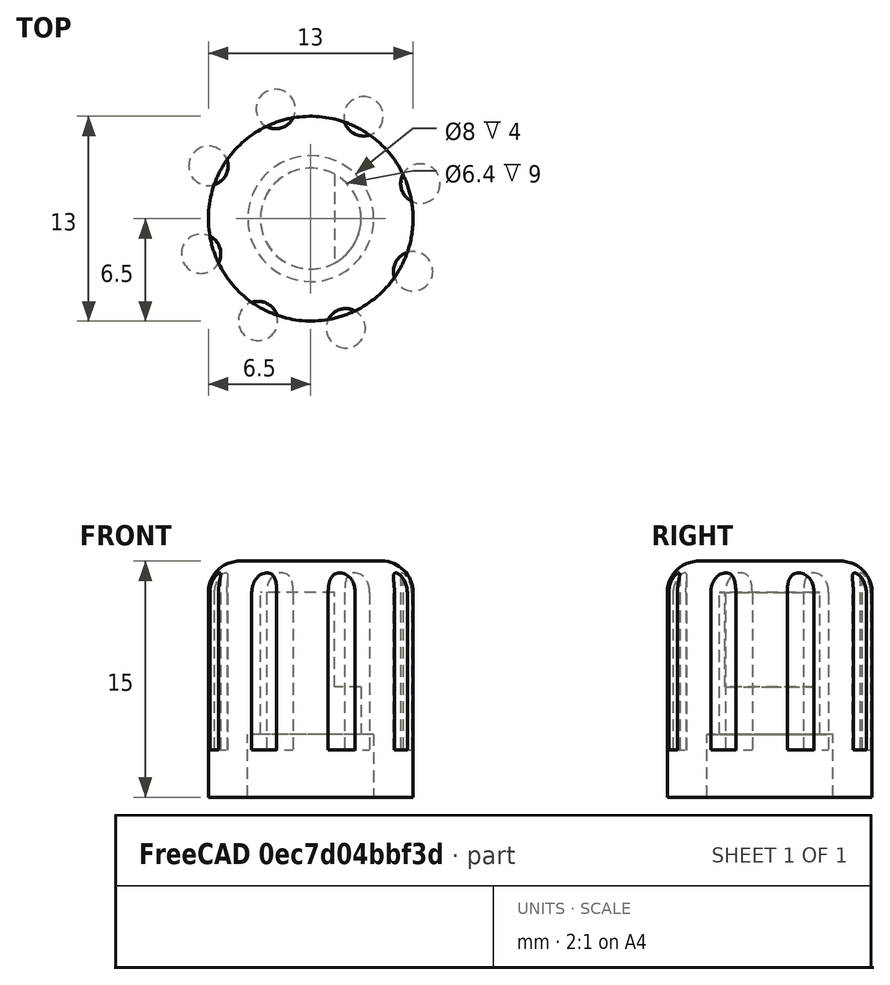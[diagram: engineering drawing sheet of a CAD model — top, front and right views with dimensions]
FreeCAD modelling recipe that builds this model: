
FCSTD DOCUMENT  (FreeCAD 0.21R33771 (Git))
Label: knob
License: All rights reserved
LicenseURL: http://en.wikipedia.org/wiki/All_rights_reserved
objects: PartDesign::SubtractiveCylinder×3, PartDesign::AdditiveCylinder×1, PartDesign::AdditiveBox×1, PartDesign::Fillet×1, PartDesign::PolarPattern×1, PartDesign::Body×1
note: 14 computed .brp shape members not serialized (recipe doc carries the construction recipe); baked Part::Feature solids carry a one-line shape summary decoded from their .brp

FEATURE [PartDesign::AdditiveCylinder] Cylinder
  Angle = 360
  AttacherType = Attacher::AttachEngine3D
  FirstAngle = 0
  Height = 15
  Radius = 6.5
  SecondAngle = 0
FEATURE [PartDesign::SubtractiveCylinder] Cylinder001
  Angle = 360
  AttacherType = Attacher::AttachEngine3D
  AttachmentOffset = pos=(0,0,-13) rot=(0,0,1;0rad)
  BaseFeature = -> Cylinder
  FirstAngle = 0
  Height = 13
  MapMode = 5
  Placement = pos=(0,0,13) rot=(1,0,0;3.14159rad)
  Radius = 3.2
  SecondAngle = 0
  Support = -> [Cylinder]
FEATURE [PartDesign::AdditiveBox] Box
  AttacherType = Attacher::AttachEngine3D
  AttachmentOffset = pos=(1.5,-3.75,-14) rot=(0,0,1;0rad)
  BaseFeature = -> Cylinder001
  Height = 7
  Length = 2
  MapMode = 5
  Placement = pos=(1.5,3.75,14) rot=(1,0,0;3.14159rad)
  Support = -> [Cylinder001]
  Width = 7.5
FEATURE [PartDesign::Fillet] Fillet
  Base = -> Box [Edge3]
  BaseFeature = -> Box
  Placement = pos=(1.5,3.75,14) rot=(1,0,0;3.14159rad)
  Radius = 2
  SupportTransform = false
  UseAllEdges = false
FEATURE [PartDesign::SubtractiveCylinder] Cylinder002
  Angle = 360
  AttacherType = Attacher::AttachEngine3D
  AttachmentOffset = pos=(-8,-0.4,-12) rot=(0,0,1;0rad)
  BaseFeature = -> Fillet
  FirstAngle = 0
  Height = 12
  MapMode = 5
  Placement = pos=(-6.5,3.35,3) rot=(0,0,1;0rad)
  Radius = 1.25
  SecondAngle = 0
  Support = -> [Fillet]
FEATURE [PartDesign::PolarPattern] PolarPattern
  Angle = 360
  Axis = -> Z_Axis
  BaseFeature = -> Cylinder002
  Occurrences = 8
  Originals = -> [Cylinder002]
  Placement = pos=(-6.5,3.35,3) rot=(0,0,1;0rad)
FEATURE [PartDesign::SubtractiveCylinder] Cylinder003
  Angle = 360
  AttacherType = Attacher::AttachEngine3D
  AttachmentOffset = pos=(6.5,3.35,3) rot=(0,0,1;0rad)
  BaseFeature = -> PolarPattern
  FirstAngle = 0
  Height = 4
  MapMode = 5
  Placement = pos=(0,-9e-16,4) rot=(1,0,0;3.14159rad)
  Radius = 4
  SecondAngle = 0
  Support = -> [PolarPattern]
FEATURE [PartDesign::Body] Body
  Group = -> [Cylinder,Cylinder001,Box,Fillet,Cylinder002,PolarPattern,Cylinder003]
  Origin = -> Origin
  Tip = -> Cylinder003
